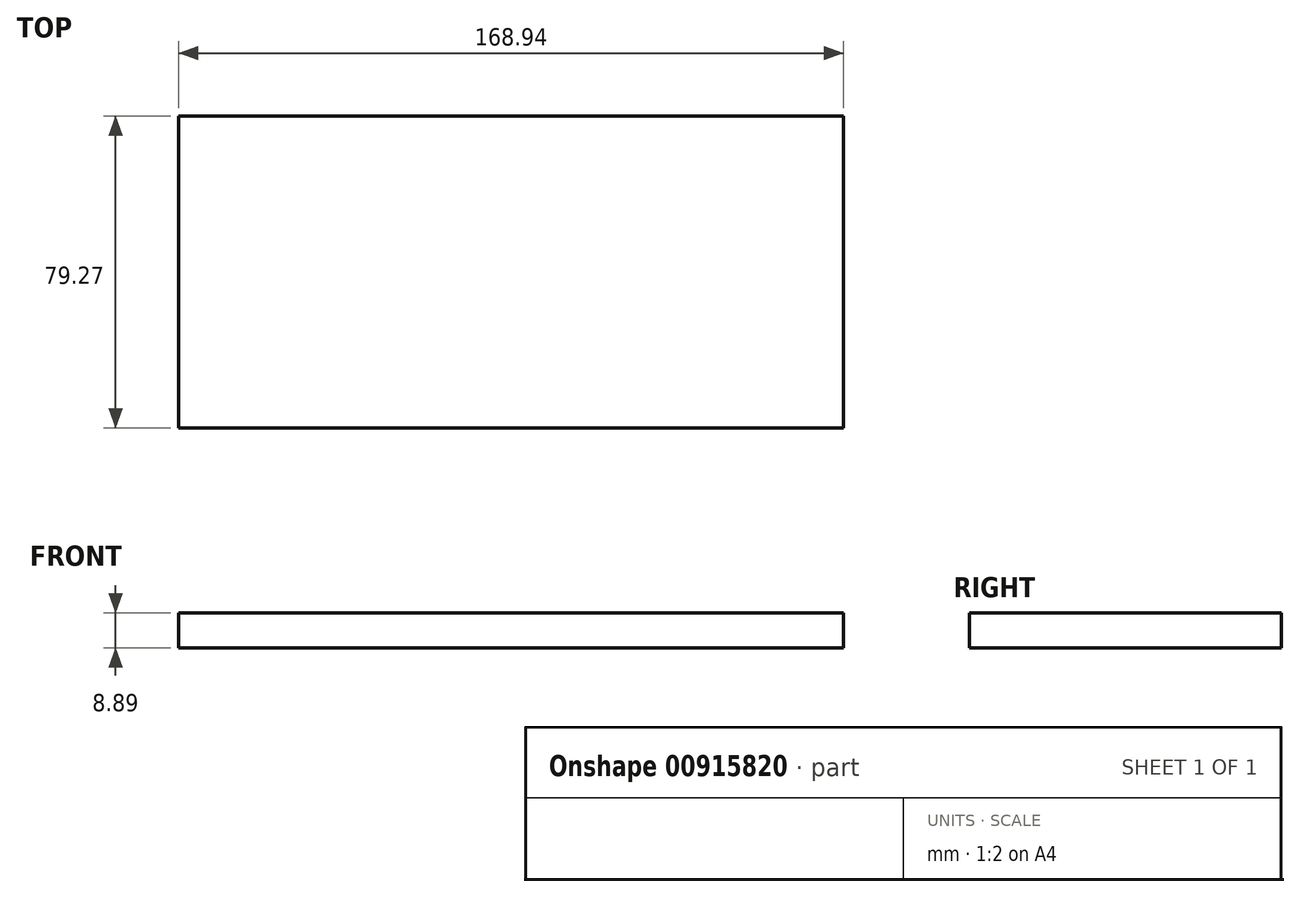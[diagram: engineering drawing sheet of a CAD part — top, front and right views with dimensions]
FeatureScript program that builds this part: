
annotation { "Feature Type Name" : "Feature", "Feature Type Description" : "" }
export const myFeature = defineFeature(function(context is Context, id is Id, definition is map)
    precondition{}
    {
        {
            var Q0;
            Q0=qCreatedBy(makeId("Top.planeOp"),FACE);
            var sketch = newSketch(context, id + "F0", { "sketchPlane" : qUnion([Q0])});
            skLineSegment(sketch, "E0.bottom", {"start": v(0, 0) * mm, "end": v(168.94, 0) * mm});
            skLineSegment(sketch, "E0.top", {"start": v(0, -79.27) * mm, "end": v(168.94, -79.27) * mm});
            skLineSegment(sketch, "E0.left", {"start": v(0, 0) * mm, "end": v(0, -79.27) * mm});
            skLineSegment(sketch, "E0.right", {"start": v(168.94, 0) * mm, "end": v(168.94, -79.27) * mm});
            skSolve(sketch);
        }
        {
            var Q0;
            Q0=makeQuery(id+"F0.imprint","IMPRINT",FACE,{"disambiguationData":[TD([[makeQuery(id+"F0.imprint","IMPRINT",EDGE,{"derivedFrom":sQuery(id+"F0.wireOp",EDGE,"E0.bottom")}),-1.0]])]});
            extrude(context, id + "F1", {"entities" : qUnion([Q0]), "depth" : 8.9 * mm, "offsetDistance" : 25.4 * mm});
        }
    });
